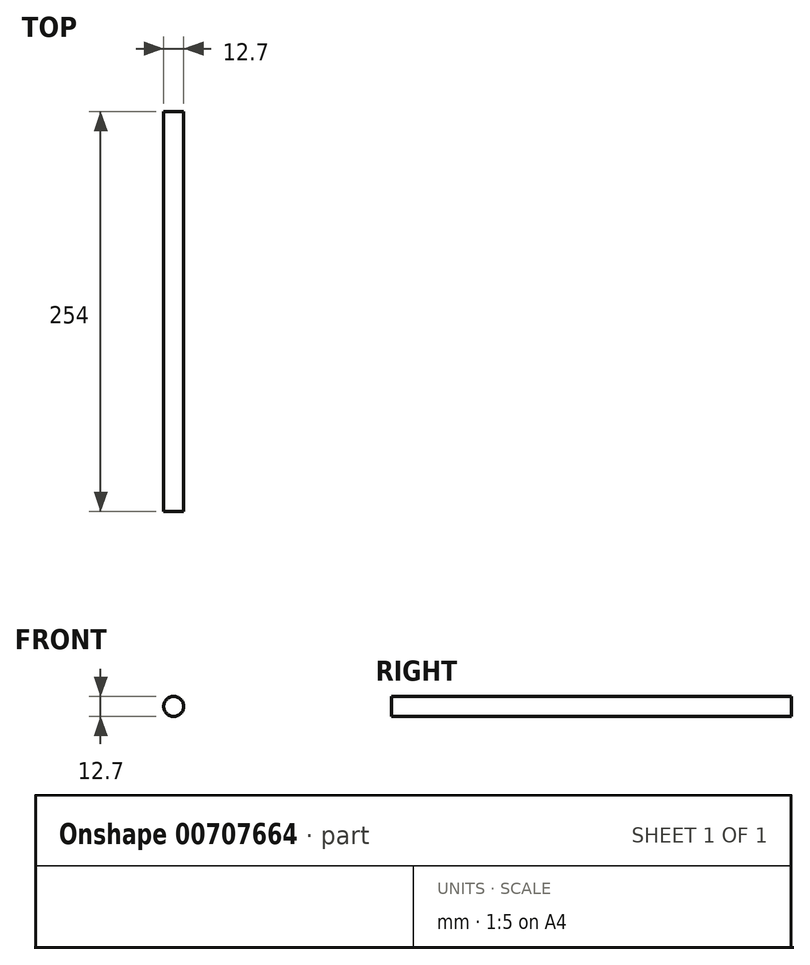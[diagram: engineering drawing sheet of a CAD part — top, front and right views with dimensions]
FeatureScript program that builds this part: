
annotation { "Feature Type Name" : "Feature", "Feature Type Description" : "" }
export const myFeature = defineFeature(function(context is Context, id is Id, definition is map)
    precondition{}
    {
        {
            var Q0;
            Q0=qCreatedBy(makeId("Front.planeOp"),FACE);
            var sketch = newSketch(context, id + "F0", { "sketchPlane" : qUnion([Q0])});
            skCircle(sketch, "E0", {"center": v(0, 0) * mm, "radius": 6.35 * mm});
            skSolve(sketch);
        }
        {
            var Q0;
            Q0 = qSketchRegion(id + "F0", true);
            extrude(context, id + "F1", {"entities" : qUnion([Q0]), "depth" : 254 * mm, "offsetDistance" : 25.4 * mm});
        }
    });
